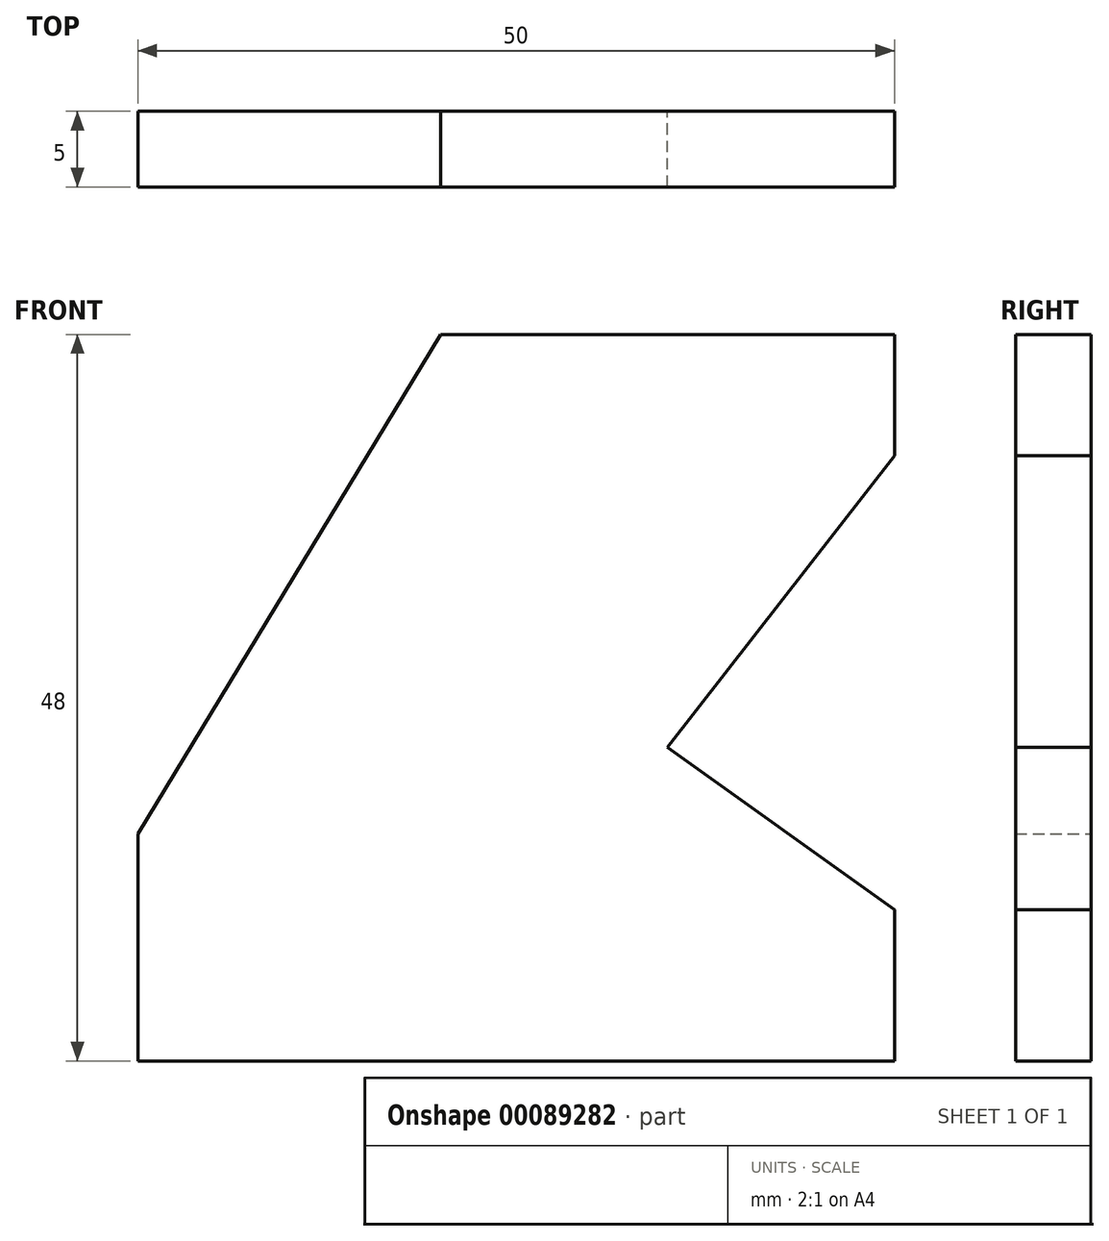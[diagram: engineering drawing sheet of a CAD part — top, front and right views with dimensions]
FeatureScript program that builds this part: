
annotation { "Feature Type Name" : "Feature", "Feature Type Description" : "" }
export const myFeature = defineFeature(function(context is Context, id is Id, definition is map)
    precondition{}
    {
        {
            var Q0;
            Q0=qCreatedBy(makeId("Front.planeOp"),FACE);
            var sketch = newSketch(context, id + "F0", { "sketchPlane" : qUnion([Q0])});
            skLineSegment(sketch, "E0", {"start": v(-30, 48) * mm, "end": v(0, 48) * mm});
            skLineSegment(sketch, "E1", {"start": v(0, 48) * mm, "end": v(0, 40) * mm});
            skLineSegment(sketch, "E2", {"start": v(0, 40) * mm, "end": v(-15, 20.72) * mm});
            skLineSegment(sketch, "E3", {"start": v(-15, 20.72) * mm, "end": v(0, 10) * mm});
            skLineSegment(sketch, "E4", {"start": v(0, 10) * mm, "end": v(0, 0) * mm});
            skLineSegment(sketch, "E5", {"start": v(0, 0) * mm, "end": v(-50, 0) * mm});
            skLineSegment(sketch, "E6", {"start": v(-50, 0) * mm, "end": v(-50, 15) * mm});
            skLineSegment(sketch, "E7", {"start": v(-50, 15) * mm, "end": v(-30, 48) * mm});
            skPoint(sketch, "E8.orphan", {"position": v(-32.93, 20.72) * mm});
            skSolve(sketch);
        }
        {
            var Q0;
            Q0=makeQuery(id+"F0.imprint","IMPRINT",FACE,{"disambiguationData":[TD([[makeQuery(id+"F0.imprint","IMPRINT",EDGE,{"derivedFrom":sQuery(id+"F0.wireOp",EDGE,"E0")}),-1.0]])]});
            extrude(context, id + "F1", {"entities" : qUnion([Q0]), "depth" : 5 * mm});
        }
    });
